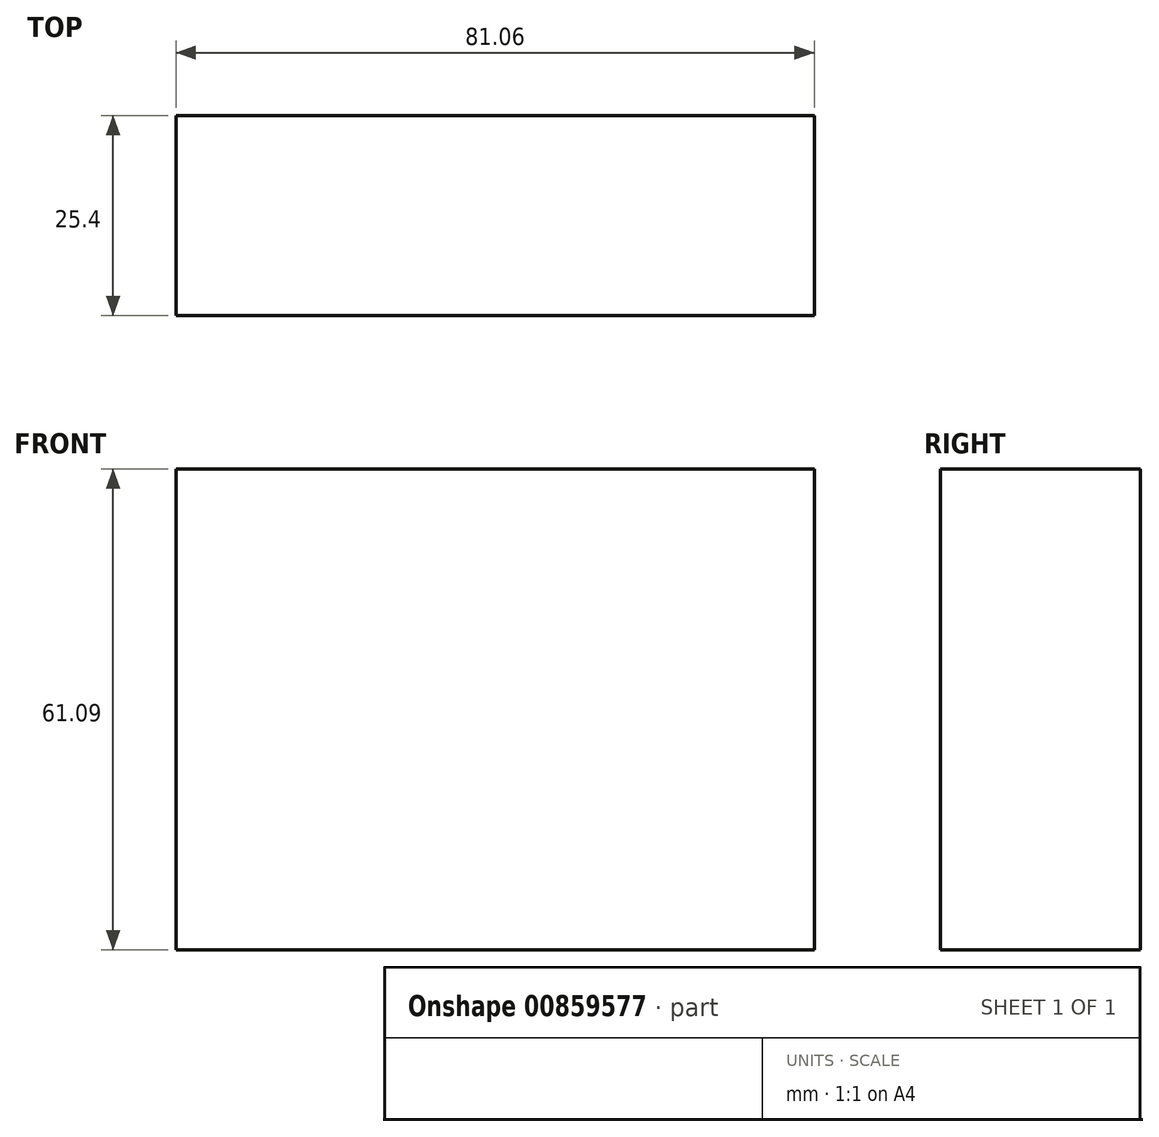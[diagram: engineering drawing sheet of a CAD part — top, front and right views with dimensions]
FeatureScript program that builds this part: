
annotation { "Feature Type Name" : "Feature", "Feature Type Description" : "" }
export const myFeature = defineFeature(function(context is Context, id is Id, definition is map)
    precondition{}
    {
        {
            var Q0;
            Q0=qCreatedBy(makeId("Front.planeOp"),FACE);
            var sketch = newSketch(context, id + "F0", { "sketchPlane" : qUnion([Q0])});
            skLineSegment(sketch, "E0.bottom", {"start": v(-142, 77.68) * mm, "end": v(-60.94, 77.68) * mm});
            skLineSegment(sketch, "E0.top", {"start": v(-142, 16.6) * mm, "end": v(-60.94, 16.6) * mm});
            skLineSegment(sketch, "E0.left", {"start": v(-142, 77.68) * mm, "end": v(-142, 16.6) * mm});
            skLineSegment(sketch, "E0.right", {"start": v(-60.94, 77.68) * mm, "end": v(-60.94, 16.6) * mm});
            skPoint(sketch, "E0.middle", {"position": v(-101.47, 47.14) * mm});
            skSolve(sketch);
        }
        {
            var Q0;
            Q0 = qSketchRegion(id + "F0", true);
            extrude(context, id + "F1", {"entities" : qUnion([Q0]), "depth" : 25.4 * mm, "offsetDistance" : 25.4 * mm});
        }
    });
